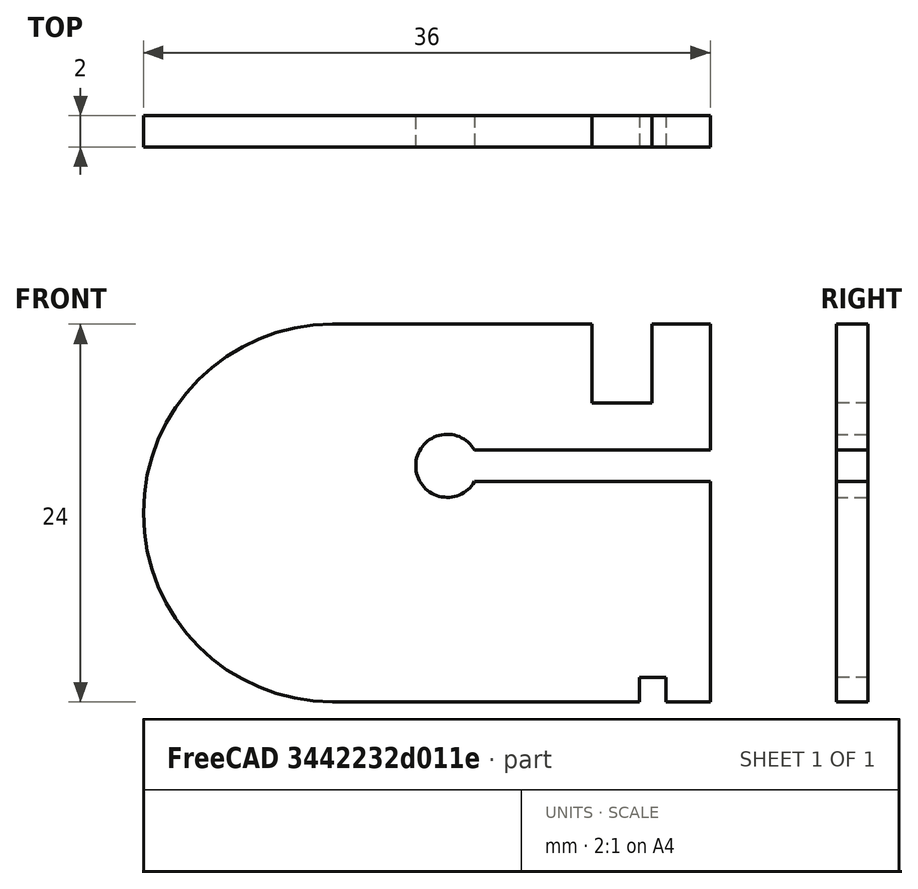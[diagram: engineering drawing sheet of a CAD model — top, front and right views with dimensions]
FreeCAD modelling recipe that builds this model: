
FCSTD DOCUMENT  (FreeCAD 1.0R)
Label: CW-Pad-Middle-Dit
License: All rights reserved
LicenseURL: https://en.wikipedia.org/wiki/All_rights_reserved
objects: Sketcher::SketchObject×1, PartDesign::Pad×1, PartDesign::Body×1, Part::Part2DObjectPython×1
note: 7 computed .brp shape members not serialized (recipe doc carries the construction recipe); baked Part::Feature solids carry a one-line shape summary decoded from their .brp

FEATURE [Sketcher::SketchObject] Sketch
  ArcFitTolerance = 1e-06
  AttachmentSupport = -> [XZ_Plane]
  FullyConstrained = true
  MakeInternals = false
  MapMode = 5
  Placement = pos=(0,0,0) rot=(1,0,0;1.5708rad)
  sketch-geometry (24):
    g0: GeomPoint [constr] X=0 Y=0 Z=0
    g1: GeomPoint [constr] X=0 Y=0 Z=0
    g2: LineSegment StartX=-15 StartY=-12 StartZ=0 EndX=4.5 EndY=-12 EndZ=0
    g3: LineSegment StartX=9 StartY=12 StartZ=0 EndX=5.3 EndY=12 EndZ=0
    g4: GeomPoint [constr] X=-3 Y=0 Z=0
    g5: ArcOfCircle CenterX=-15 CenterY=4e-16 CenterZ=0 NormalX=0 NormalY=0 NormalZ=1 AngleXU=0 Radius=12 StartAngle=1.5708 EndAngle=4.71239
    g6: LineSegment StartX=6.2 StartY=-12 StartZ=0 EndX=6.2 EndY=-10.45 EndZ=0
    g7: LineSegment StartX=6.2 StartY=-10.45 StartZ=0 EndX=4.5 EndY=-10.45 EndZ=0
    g8: LineSegment StartX=4.5 StartY=-10.45 StartZ=0 EndX=4.5 EndY=-12 EndZ=0
    g9: GeomPoint [constr] X=5.35 Y=-11.225 Z=0
    g10: LineSegment StartX=6.2 StartY=-12 StartZ=0 EndX=9 EndY=-12 EndZ=0
    g11: LineSegment StartX=1.5 StartY=7 StartZ=0 EndX=5.3 EndY=7 EndZ=0
    g12: LineSegment StartX=5.3 StartY=7 StartZ=0 EndX=5.3 EndY=12 EndZ=0
    g13: LineSegment StartX=1.5 StartY=12 StartZ=0 EndX=1.5 EndY=7 EndZ=0
    g14: GeomPoint [constr] X=3.4 Y=9.5 Z=0
    g15: LineSegment StartX=1.5 StartY=12 StartZ=0 EndX=-15 EndY=12 EndZ=0
    g16: Circle [constr] CenterX=-15 CenterY=4e-16 CenterZ=0 NormalX=0 NormalY=0 NormalZ=1 AngleXU=0 Radius=9.875
    g17: LineSegment [constr] StartX=1.5 StartY=30 StartZ=0 EndX=1.5 EndY=-30 EndZ=0
    g18: LineSegment StartX=-5.9714 StartY=2 StartZ=0 EndX=9 EndY=2 EndZ=0
    g19: LineSegment StartX=9 StartY=4 StartZ=0 EndX=-5.9714 EndY=4 EndZ=0
    g20: GeomPoint [constr] X=1.5143 Y=3 Z=0
    g21: LineSegment StartX=9 StartY=-12 StartZ=0 EndX=9 EndY=2 EndZ=0
    g22: LineSegment StartX=9 StartY=12 StartZ=0 EndX=9 EndY=4 EndZ=0
    g23: ArcOfCircle CenterX=-7.70345 CenterY=3 CenterZ=0 NormalX=0 NormalY=0 NormalZ=1 AngleXU=0 Radius=2 StartAngle=0.523599 EndAngle=5.75959
  constraints (61):
    c: Coincident(g0,g-1)
    c: Coincident(g1,g0)
    c: Horizontal(g2)
    c: Horizontal(g3)
    c: Symmetric(g3,g2,g4)
    c: Distance(g2,g15) = 24
    c: Horizontal(g4,g0)
    c: Coincident(g5,g2)
    c: Coincident(g5,g15)
    c: DistanceX(g5,g0) = 15
    c: Coincident(g6,g7)
    c: Coincident(g7,g8)
    c: Horizontal(g7)
    c: Vertical(g6)
    c: Vertical(g8)
    c: Symmetric(g7,g8,g9)
    c: DistanceX(g0,g8) = 4.5
    c: Equal(g8,g6)
    c: Parallel(g10,g2)
    c: Coincident(g6,g10)
    c: Coincident(g8,g2)
    c: Coincident(g11,g12)
    c: Coincident(g13,g11)
    c: Horizontal(g11)
    c: Vertical(g12)
    c: Vertical(g13)
    c: Symmetric(g12,g11,g14)
    c: DistanceX(g0,g13) = 1.5
    c: Coincident(g15,g13)
    c: Parallel(g15,g2)
    c: DistanceX(g13,g3) = 3.8
    c: Diameter(g16) = 19.75
    c: Coincident(g16,g5)
    c: DistanceY(g17,g17) = 60
    c: DistanceX(g0,g17) = 1.5
    c: Symmetric(g17,g17,g-1)
    c: DistanceY(g2,g7) = 1.55
    c: DistanceX(g2,g6) = 1.7
    c: Symmetric(g5,g2,g-1)
    c: DistanceX(g0,g3) = 9
    c: Coincident(g12,g3)
    c: DistanceY(g11,g3) = 5
    c: Vertical(g5,g5)
    c: Horizontal(g18)
    c: Horizontal(g19)
    c: Symmetric(g18,g19,g20)
    c: DistanceY(g-1,g20) = 3
    c: Vertical(g3,g19)
    c: Coincident(g21,g10)
    c: Coincident(g21,g18)
    c: Vertical(g21)
    c: Coincident(g22,g3)
    c: Coincident(g22,g19)
    c: Vertical(g3,g10)
    c: DistanceY(g18,g19) = 2
    c: Vertical(g19,g18)
    c: Horizontal(g23,g20)
    c: Diameter(g23) = 4
    c: Coincident(g23,g18)
    c: Vertical(g23,g19)
    c: PointOnObject(g19,g16)
FEATURE [PartDesign::Pad] Pad
  Direction = (0,-1,2e-16)
  Length = 2
  Length2 = 10
  Midplane = true
  Placement = pos=(0,0,0) rot=(1,0,0;1.5708rad)
  Profile = -> Sketch
  ReferenceAxis = -> Sketch [N_Axis]
  Refine = true
  Suppressed = false
  Type = 0
FEATURE [PartDesign::Body] Body  label="CW-Pad-Middle-Dit"
  AllowCompound = false
  Group = -> [Sketch,Pad]
  Origin = -> Origin
  Tip = -> Pad
FEATURE [Part::Part2DObjectPython] Shape2DView  # Draft 2D object (typed FeaturePython)
  AutoUpdate = true
  Base = -> Pad
  Clip = false
  FuseArch = false
  HiddenLines = false
  InPlace = true
  OnlySolids = false
  Projection = (0,-1,0)
  ProjectionMode = 0
  SegmentLength = 0.05
  Tessellation = false
  VisibleOnly = false
